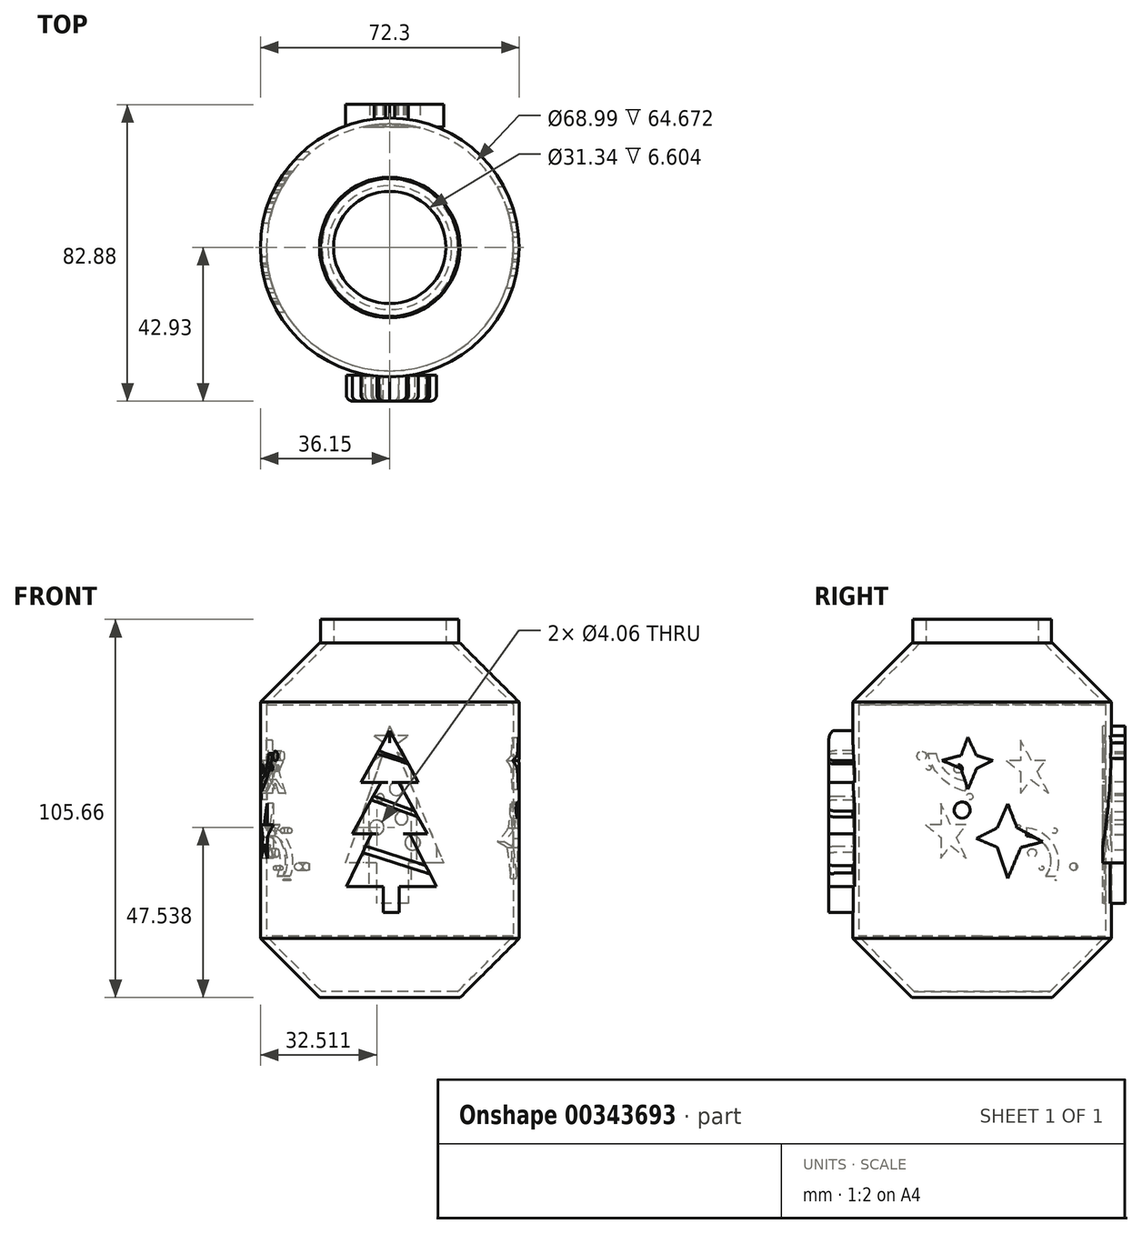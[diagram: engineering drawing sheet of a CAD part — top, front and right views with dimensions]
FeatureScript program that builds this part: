
annotation { "Feature Type Name" : "Feature", "Feature Type Description" : "" }
export const myFeature = defineFeature(function(context is Context, id is Id, definition is map)
    precondition{}
    {
        {
            var Q0;
            Q0=qCreatedBy(makeId("Top.planeOp"),FACE);
            var sketch = newSketch(context, id + "F0", { "sketchPlane" : qUnion([Q0])});
            skCircle(sketch, "E0", {"center": v(0, 0) * mm, "radius": 27.8 * mm});
            skSolve(sketch);
        }
        {
            var Q0;
            Q0=makeQuery(id+"F0.imprint","IMPRINT",FACE,{"disambiguationData":[TD([[makeQuery(id+"F0.imprint","IMPRINT",EDGE,{"derivedFrom":sQuery(id+"F0.wireOp",EDGE,"E0")}),1.0]])]});
            extrude(context, id + "F1", {"entities" : qUnion([Q0]), "depth" : 76.2 * mm});
        }
        {
            var Q0;
            Q0=makeQuery(id+"F1.opExtrude","CAP_EDGE",EDGE,{"disambiguationData":[OSD([sQuery(id+"F0.wireOp",EDGE,"E0")])],"isStart":false});
            var Q1;
            Q1=makeQuery(id+"F1.opExtrude","SWEPT_FACE",FACE,{"disambiguationData":[OSD([sQuery(id+"F0.wireOp",EDGE,"E0")])]});
            chamfer(context, id + "F2", {"entities" : qUnion([Q0, Q1]), "width" : 12.7 * mm, "tangentPropagation" : true});
        }
        {
            var Q0;
            Q0=makeQuery(id+"F1.opExtrude","CAP_FACE",FACE,{"disambiguationData":[OSD([sQuery(id+"F0.wireOp",EDGE,"E0")])],"isStart":false});
            shell(context, id + "F3", {"entities" : qUnion([Q0]), "thickness" : 1.27 * mm});
        }
        {
            var Q0;
            Q0=qCreatedBy(makeId("Front.planeOp"),FACE);
            cPlane(context, id + "F4", {"entities" : qUnion([Q0]), "cplaneType" : CPlaneType.OFFSET, "offset" : 27.43 * mm, "width" : 152.4 * mm, "height" : 152.4 * mm});
        }
        {
            var Q0;
            Q0=qCreatedBy(id+"F4.planeOp",FACE);
            var sketch = newSketch(context, id + "F5", { "sketchPlane" : qUnion([Q0])});
            skLineSegment(sketch, "E1", {"start": v(0, 57.39) * mm, "end": v(-6.16, 46.28) * mm});
            skLineSegment(sketch, "E2", {"start": v(-6.16, 46.28) * mm, "end": v(-1.9, 46.28) * mm});
            skLineSegment(sketch, "E3", {"start": v(6.16, 46.28) * mm, "end": v(0, 57.39) * mm});
            skLineSegment(sketch, "E4", {"start": v(-1.9, 46.28) * mm, "end": v(-8.05, 35.18) * mm});
            skLineSegment(sketch, "E5", {"start": v(-8.05, 35.18) * mm, "end": v(-3.9, 35.18) * mm});
            skLineSegment(sketch, "E6", {"start": v(8.05, 35.18) * mm, "end": v(1.9, 46.28) * mm});
            skPoint(sketch, "E7.orphan", {"position": v(0, 49.7) * mm});
            skLineSegment(sketch, "E8.trimOffspring", {"start": v(1.9, 46.28) * mm, "end": v(6.16, 46.28) * mm});
            skLineSegment(sketch, "E9", {"start": v(-3.9, 35.18) * mm, "end": v(-9.31, 23.85) * mm});
            skLineSegment(sketch, "E10", {"start": v(4.3, 35.18) * mm, "end": v(10.03, 23.85) * mm});
            skLineSegment(sketch, "E11", {"start": v(10.03, 23.85) * mm, "end": v(2.04, 23.85) * mm});
            skLineSegment(sketch, "E12.trimOffspring", {"start": v(4.3, 35.18) * mm, "end": v(8.05, 35.18) * mm});
            skLineSegment(sketch, "E13.top", {"start": v(2.04, 18.3) * mm, "end": v(-1.34, 18.3) * mm});
            skLineSegment(sketch, "E13.left", {"start": v(2.04, 23.85) * mm, "end": v(2.04, 18.3) * mm});
            skLineSegment(sketch, "E13.right", {"start": v(-1.34, 23.85) * mm, "end": v(-1.34, 18.3) * mm});
            skLineSegment(sketch, "E14.trimOffspring", {"start": v(-1.34, 23.85) * mm, "end": v(-9.31, 23.85) * mm});
            skSolve(sketch);
        }
        {
            var Q0;
            Q0 = qSketchRegion(id + "F5", true);
            extrude(context, id + "F6", {"entities" : qUnion([Q0]), "operationType" : NewBodyOperationType.ADD, "depth" : 5.6 * mm});
        }
        {
            var Q0;
            Q0=makeQuery(id+"F6.opExtrude","CAP_EDGE",EDGE,{"disambiguationData":[OSD([sQuery(id+"F5.wireOp",EDGE,"E3")])],"isStart":false});
            var Q1;
            Q1=makeQuery(id+"F6.opExtrude","CAP_EDGE",EDGE,{"disambiguationData":[OSD([sQuery(id+"F5.wireOp",EDGE,"E1")])],"isStart":false});
            var Q2;
            Q2=makeQuery(id+"F6.opExtrude","CAP_EDGE",EDGE,{"disambiguationData":[OSD([sQuery(id+"F5.wireOp",EDGE,"E9")])],"isStart":false});
            var Q3;
            Q3=makeQuery(id+"F6.opExtrude","CAP_EDGE",EDGE,{"disambiguationData":[OSD([sQuery(id+"F5.wireOp",EDGE,"E4")])],"isStart":false});
            var Q4;
            Q4=makeQuery(id+"F6.opExtrude","CAP_EDGE",EDGE,{"disambiguationData":[OSD([sQuery(id+"F5.wireOp",EDGE,"E6")])],"isStart":false});
            var Q5;
            Q5=makeQuery(id+"F6.opExtrude","CAP_EDGE",EDGE,{"disambiguationData":[OSD([sQuery(id+"F5.wireOp",EDGE,"E10")])],"isStart":false});
            fillet(context, id + "F7", {"entities" : qUnion([Q0, Q1, Q2, Q3, Q4, Q5]), "radius" : 1.27 * mm, "tangentPropagation" : true, "allowEdgeOverflow" : false});
        }
        {
            var Q0;
            Q0=qCreatedBy(id+"F4.planeOp",FACE);
            var Q1;
            Q1 = qBodyType(qCreatedBy(id + "F9" ,EDGE), BodyType.WIRE);
            cPlane(context, id + "F8", {"entities" : qUnion([Q0, Q1]), "cplaneType" : CPlaneType.OFFSET, "offset" : 5.84 * mm, "width" : 152.4 * mm, "height" : 152.4 * mm});
        }
        {
            var Q0;
            Q0=qCreatedBy(id+"F8.planeOp",FACE);
            var sketch = newSketch(context, id + "F9", { "sketchPlane" : qUnion([Q0])});
            skLineSegment(sketch, "E15", {"start": v(-2.4, 53.07) * mm, "end": v(3.58, 50.94) * mm});
            skLineSegment(sketch, "E16", {"start": v(3.58, 50.94) * mm, "end": v(4, 50.2) * mm});
            skLineSegment(sketch, "E17", {"start": v(4, 50.2) * mm, "end": v(-2.76, 52.43) * mm});
            skLineSegment(sketch, "E18", {"start": v(-2.76, 52.43) * mm, "end": v(-2.4, 53.07) * mm});
            skLineSegment(sketch, "E19.0", {"start": v(0, 57.39) * mm, "end": v(6.16, 46.28) * mm});
            skLineSegment(sketch, "E20", {"start": v(-3.54, 43.37) * mm, "end": v(5.35, 40.1) * mm});
            skLineSegment(sketch, "E21", {"start": v(5.35, 40.1) * mm, "end": v(6.1, 38.81) * mm});
            skLineSegment(sketch, "E22", {"start": v(6.1, 38.81) * mm, "end": v(-4.02, 42.49) * mm});
            skLineSegment(sketch, "E23", {"start": v(-4.02, 42.49) * mm, "end": v(-3.54, 43.37) * mm});
            skLineSegment(sketch, "E24", {"start": v(-5.18, 32.56) * mm, "end": v(7.86, 28.32) * mm});
            skLineSegment(sketch, "E25", {"start": v(7.86, 28.32) * mm, "end": v(8.64, 26.56) * mm});
            skLineSegment(sketch, "E26", {"start": v(8.64, 26.56) * mm, "end": v(-5.84, 31.16) * mm});
            skLineSegment(sketch, "E27", {"start": v(-5.84, 31.16) * mm, "end": v(-5.18, 32.56) * mm});
            skSolve(sketch);
        }
        {
            var Q0;
            Q0 = qSketchRegion(id + "F9", true);
            extrude(context, id + "F10", {"entities" : qUnion([Q0]), "operationType" : NewBodyOperationType.REMOVE, "oppositeDirection" : true, "depth" : 5.6 * mm});
        }
        {
            var Q0;
            Q0=qCreatedBy(makeId("Right.planeOp"),FACE);
            cPlane(context, id + "F11", {"entities" : qUnion([Q0]), "cplaneType" : CPlaneType.OFFSET, "offset" : 28.2 * mm, "width" : 152.4 * mm, "height" : 152.4 * mm});
        }
        {
            var Q0;
            Q0=qCreatedBy(id+"F11.planeOp",FACE);
            var sketch = newSketch(context, id + "F12", { "sketchPlane" : qUnion([Q0])});
            skLineSegment(sketch, "E28", {"start": v(-3.07, 55.96) * mm, "end": v(-4.52, 52.05) * mm});
            skLineSegment(sketch, "E29", {"start": v(-4.52, 52.05) * mm, "end": v(-8.66, 50.98) * mm});
            skLineSegment(sketch, "E30", {"start": v(-8.66, 50.98) * mm, "end": v(-4.52, 49.22) * mm});
            skLineSegment(sketch, "E31", {"start": v(-4.52, 49.22) * mm, "end": v(-3.07, 44.74) * mm});
            skLineSegment(sketch, "E32", {"start": v(-3.07, 44.74) * mm, "end": v(-1.23, 49.22) * mm});
            skLineSegment(sketch, "E33", {"start": v(-1.23, 49.22) * mm, "end": v(2.26, 50.98) * mm});
            skLineSegment(sketch, "E34", {"start": v(2.26, 50.98) * mm, "end": v(-1.23, 52.05) * mm});
            skLineSegment(sketch, "E35", {"start": v(-1.23, 52.05) * mm, "end": v(-3.07, 55.96) * mm});
            skLineSegment(sketch, "E36", {"start": v(5.5, 41.67) * mm, "end": v(3.3, 36.5) * mm});
            skLineSegment(sketch, "E37", {"start": v(3.3, 36.5) * mm, "end": v(-1.23, 34.22) * mm});
            skLineSegment(sketch, "E38", {"start": v(-1.23, 34.22) * mm, "end": v(3.3, 32.29) * mm});
            skLineSegment(sketch, "E39", {"start": v(3.3, 32.29) * mm, "end": v(5.5, 25.62) * mm});
            skLineSegment(sketch, "E40", {"start": v(5.5, 25.62) * mm, "end": v(8.34, 32.29) * mm});
            skLineSegment(sketch, "E41", {"start": v(8.34, 32.29) * mm, "end": v(13.05, 33.5) * mm});
            skLineSegment(sketch, "E42", {"start": v(13.05, 33.5) * mm, "end": v(7.5, 36.5) * mm});
            skLineSegment(sketch, "E43", {"start": v(7.5, 36.5) * mm, "end": v(5.5, 41.67) * mm});
            skCircle(sketch, "E44", {"center": v(-4.3, 40.3) * mm, "radius": 1.73 * mm});
            skSolve(sketch);
        }
        {
            var Q0;
            Q0 = qSketchRegion(id + "F12", true);
            extrude(context, id + "F13", {"entities" : qUnion([Q0]), "operationType" : NewBodyOperationType.REMOVE, "oppositeDirection" : true, "depth" : 6.1 * mm});
        }
        {
            var Q0;
            Q0=qCreatedBy(makeId("Front.planeOp"),FACE);
            cPlane(context, id + "F14", {"entities" : qUnion([Q0]), "cplaneType" : CPlaneType.OFFSET, "offset" : 25.9 * mm, "oppositeDirection" : true, "width" : 152.4 * mm, "height" : 152.4 * mm});
        }
        {
            var Q0;
            Q0=qCreatedBy(id+"F14.planeOp",FACE);
            var sketch = newSketch(context, id + "F15", { "sketchPlane" : qUnion([Q0])});
            skLineSegment(sketch, "E45", {"start": v(1.57, 52.8) * mm, "end": v(11.56, 28.93) * mm});
            skLineSegment(sketch, "E46", {"start": v(11.56, 28.93) * mm, "end": v(-9.45, 28.93) * mm});
            skLineSegment(sketch, "E47", {"start": v(-9.45, 28.93) * mm, "end": v(-1.42, 52.39) * mm});
            skLineSegment(sketch, "E48", {"start": v(3.93, 28.93) * mm, "end": v(3.93, 20.27) * mm});
            skLineSegment(sketch, "E49", {"start": v(3.93, 20.27) * mm, "end": v(-2.85, 20.27) * mm});
            skLineSegment(sketch, "E50", {"start": v(-2.85, 20.27) * mm, "end": v(-2.85, 28.93) * mm});
            skLineSegment(sketch, "E51", {"start": v(4, 56.28) * mm, "end": v(1.06, 56.28) * mm});
            skLineSegment(sketch, "E52", {"start": v(-3.36, 56.28) * mm, "end": v(-1.5, 54.97) * mm});
            skLineSegment(sketch, "E53", {"start": v(3.54, 51.4) * mm, "end": v(1.85, 54.74) * mm});
            skLineSegment(sketch, "E54", {"start": v(0, 58.36) * mm, "end": v(-0.92, 56.28) * mm});
            skLineSegment(sketch, "E55", {"start": v(-3.2, 51.1) * mm, "end": v(-1.42, 52.39) * mm});
            skLineSegment(sketch, "E56.trimOffspring", {"start": v(1.06, 56.28) * mm, "end": v(0, 58.36) * mm});
            skLineSegment(sketch, "E57.trimOffspring", {"start": v(-0.92, 56.28) * mm, "end": v(-3.36, 56.28) * mm});
            skPoint(sketch, "E58.orphan", {"position": v(0, 56.54) * mm});
            skLineSegment(sketch, "E59.trimOffspring", {"start": v(-1.5, 54.97) * mm, "end": v(-3.2, 51.1) * mm});
            skLineSegment(sketch, "E60.trimOffspring", {"start": v(1.57, 52.8) * mm, "end": v(3.54, 51.4) * mm});
            skLineSegment(sketch, "E61.trimOffspring", {"start": v(1.85, 54.74) * mm, "end": v(4, 56.28) * mm});
            skCircle(sketch, "E62", {"center": v(1.43, 44.91) * mm, "radius": 1.47 * mm});
            skCircle(sketch, "E63", {"center": v(-2.8, 36.57) * mm, "radius": 1.56 * mm});
            skCircle(sketch, "E64", {"center": v(4.9, 33.32) * mm, "radius": 1.61 * mm});
            skCircle(sketch, "E65", {"center": v(2.51, 38.52) * mm, "radius": 1.37 * mm});
            skCircle(sketch, "E66", {"center": v(-2.03, 43) * mm, "radius": 0.81 * mm});
            skSolve(sketch);
        }
        {
            var Q0;
            Q0 = qSketchRegion(id + "F15", true);
            extrude(context, id + "F16", {"entities" : qUnion([Q0]), "operationType" : NewBodyOperationType.ADD, "oppositeDirection" : true, "depth" : 4.83 * mm});
        }
        {
            var Q0;
            Q0=qCreatedBy(makeId("Right.planeOp"),FACE);
            cPlane(context, id + "F17", {"entities" : qUnion([Q0]), "cplaneType" : CPlaneType.OFFSET, "offset" : 27.94 * mm, "oppositeDirection" : true, "width" : 152.4 * mm, "height" : 152.4 * mm});
        }
        {
            var Q0;
            Q0=qCreatedBy(id+"F17.planeOp",FACE);
            var sketch = newSketch(context, id + "F18", { "sketchPlane" : qUnion([Q0])});
            skLineSegment(sketch, "E67", {"start": v(5.15, 50.93) * mm, "end": v(8.21, 50.93) * mm});
            skLineSegment(sketch, "E68", {"start": v(13.58, 50.93) * mm, "end": v(11.82, 48.61) * mm});
            skLineSegment(sketch, "E69", {"start": v(8.21, 43.88) * mm, "end": v(8.21, 48.58) * mm});
            skLineSegment(sketch, "E70", {"start": v(8.21, 55.37) * mm, "end": v(10.58, 50.93) * mm});
            skLineSegment(sketch, "E71", {"start": v(14.34, 43.88) * mm, "end": v(10.47, 46.85) * mm});
            skLineSegment(sketch, "E72", {"start": v(-12.17, 37.13) * mm, "end": v(-8.9, 37.13) * mm});
            skLineSegment(sketch, "E73", {"start": v(-3.44, 37.13) * mm, "end": v(-5.5, 34.42) * mm});
            skLineSegment(sketch, "E74", {"start": v(-8.9, 29.96) * mm, "end": v(-8.9, 34.44) * mm});
            skLineSegment(sketch, "E75", {"start": v(-8.9, 41.73) * mm, "end": v(-6.76, 37.13) * mm});
            skLineSegment(sketch, "E76", {"start": v(-3.44, 29.96) * mm, "end": v(-6.8, 32.72) * mm});
            skLineSegment(sketch, "E77.trimOffspring", {"start": v(11.82, 48.61) * mm, "end": v(14.34, 43.88) * mm});
            skLineSegment(sketch, "E78.trimOffspring", {"start": v(10.58, 50.93) * mm, "end": v(13.58, 50.93) * mm});
            skLineSegment(sketch, "E79.trimOffspring", {"start": v(8.21, 50.93) * mm, "end": v(8.21, 55.37) * mm});
            skLineSegment(sketch, "E80.trimOffspring", {"start": v(8.21, 48.58) * mm, "end": v(5.15, 50.93) * mm});
            skLineSegment(sketch, "E81.trimOffspring", {"start": v(10.47, 46.85) * mm, "end": v(8.21, 43.88) * mm});
            skLineSegment(sketch, "E82.trimOffspring", {"start": v(-6.76, 37.13) * mm, "end": v(-3.44, 37.13) * mm});
            skLineSegment(sketch, "E83.trimOffspring", {"start": v(-5.5, 34.42) * mm, "end": v(-3.44, 29.96) * mm});
            skLineSegment(sketch, "E84.trimOffspring", {"start": v(-6.8, 32.72) * mm, "end": v(-8.9, 29.96) * mm});
            skLineSegment(sketch, "E85.trimOffspring", {"start": v(-8.9, 34.44) * mm, "end": v(-12.17, 37.13) * mm});
            skLineSegment(sketch, "E86.trimOffspring", {"start": v(-8.9, 37.13) * mm, "end": v(-8.9, 41.73) * mm});
            skArc(sketch, "E87", {"start": v(-9.8, 52.5) * mm, "mid": v(-7.7, 48.55) * mm, "end": v(-3.73, 46.52) * mm});
            skArc(sketch, "E88", {"start": v(-9.8, 52.5) * mm, "mid": v(-10.73, 52.55) * mm, "end": v(-11.65, 52.5) * mm});
            skArc(sketch, "E89", {"start": v(-3.73, 44.35) * mm, "mid": v(-3.55, 45.44) * mm, "end": v(-3.73, 46.52) * mm});
            skArc(sketch, "E90", {"start": v(-11.65, 52.5) * mm, "mid": v(-8.83, 47.3) * mm, "end": v(-3.73, 44.35) * mm});
            skArc(sketch, "E91", {"start": v(15.72, 26.16) * mm, "mid": v(15.3, 32.97) * mm, "end": v(9.51, 36.59) * mm});
            skLineSegment(sketch, "E92", {"start": v(9.51, 36.59) * mm, "end": v(9.51, 34.73) * mm});
            skLineSegment(sketch, "E93", {"start": v(15.72, 26.16) * mm, "end": v(13.63, 26.16) * mm});
            skArc(sketch, "E94", {"start": v(13.63, 26.16) * mm, "mid": v(14.19, 31.7) * mm, "end": v(9.51, 34.73) * mm});
            skArc(sketch, "E95", {"start": v(15.74, 25.4) * mm, "mid": v(15.78, 25.27) * mm, "end": v(15.84, 25.14) * mm});
            skPoint(sketch, "E96.center.orphan", {"position": v(-14.08, 54.82) * mm});
            skPoint(sketch, "E97.center.orphan", {"position": v(-11.9, 54.82) * mm});
            skPoint(sketch, "E98.center.orphan", {"position": v(-9.8, 54.28) * mm});
            skArc(sketch, "E99.trimOffspring", {"start": v(15.84, 25.14) * mm, "mid": v(15.8, 25.28) * mm, "end": v(15.74, 25.4) * mm});
            skCircle(sketch, "E100", {"center": v(12.76, 27.85) * mm, "radius": 0.47 * mm});
            skCircle(sketch, "E101", {"center": v(15.55, 35.88) * mm, "radius": 0.59 * mm});
            skCircle(sketch, "E102", {"center": v(7.86, 36.78) * mm, "radius": 0.36 * mm});
            skCircle(sketch, "E103", {"center": v(19.68, 28.14) * mm, "radius": 0.8 * mm});
            skCircle(sketch, "E104", {"center": v(10.73, 31.1) * mm, "radius": 0.92 * mm});
            skCircle(sketch, "E105", {"center": v(-5.13, 49.15) * mm, "radius": 0.9 * mm});
            skCircle(sketch, "E106", {"center": v(-11.5, 49.4) * mm, "radius": 0.52 * mm});
            skCircle(sketch, "E107", {"center": v(-12.99, 51.94) * mm, "radius": 1.01 * mm});
            skCircle(sketch, "E108", {"center": v(-2.7, 43.2) * mm, "radius": 0.7 * mm});
            skSolve(sketch);
        }
        {
            var Q0;
            Q0 = qSketchRegion(id + "F18", true);
            extrude(context, id + "F19", {"entities" : qUnion([Q0]), "operationType" : NewBodyOperationType.REMOVE, "depth" : 10.67 * mm});
        }
        {
            var Q0;
            Q0=qCreatedBy(id+"F14.planeOp",FACE);
            var sketch = newSketch(context, id + "F20", { "sketchPlane" : qUnion([Q0])});
            skCircle(sketch, "E109.0", {"center": v(-2.03, 43) * mm, "radius": 0.81 * mm});
            skCircle(sketch, "E110.0", {"center": v(1.43, 44.91) * mm, "radius": 1.47 * mm});
            skCircle(sketch, "E111.0", {"center": v(2.51, 38.52) * mm, "radius": 1.37 * mm});
            skCircle(sketch, "E112.0", {"center": v(-2.8, 36.57) * mm, "radius": 1.56 * mm});
            skCircle(sketch, "E113.0", {"center": v(4.9, 33.32) * mm, "radius": 1.61 * mm});
            skSolve(sketch);
        }
        {
            var Q0;
            Q0 = qSketchRegion(id + "F20", true);
            extrude(context, id + "F21", {"entities" : qUnion([Q0]), "operationType" : NewBodyOperationType.REMOVE, "depth" : 7.62 * mm});
        }
        {
            var Q0;
            Q0=qCreatedBy(makeId("Top.planeOp"),FACE);
            cPlane(context, id + "F22", {"entities" : qUnion([Q0]), "cplaneType" : CPlaneType.OFFSET, "offset" : 76.2 * mm, "width" : 152.4 * mm, "height" : 152.4 * mm});
        }
        {
            var Q0;
            Q0=qCreatedBy(id+"F22.planeOp",FACE);
            var sketch = newSketch(context, id + "F23", { "sketchPlane" : qUnion([Q0])});
            skCircle(sketch, "E114", {"center": v(0, 0) * mm, "radius": 12.06 * mm});
            skCircle(sketch, "E115", {"center": v(0, 0) * mm, "radius": 14.86 * mm});
            skSolve(sketch);
        }
        {
            var Q0;
            Q0 = qSketchRegion(id + "F23", true);
            extrude(context, id + "F24", {"entities" : qUnion([Q0]), "operationType" : NewBodyOperationType.ADD, "depth" : 5.08 * mm});
        }
        {
            var Q0;
            Q0=makeQuery(id+"F1.opExtrude","SWEPT_BODY",BODY,{"disambiguationData":[OSD([sQuery(id+"F0.wireOp",EDGE,"E0")])]});
            var Q1;
            Q1=qCreatedBy(makeId("Origin.pointOp"),VERTEX);
            transform(context, id + "F25", {"entities" : qUnion([Q0]), "transformType" : TransformType.SCALE_UNIFORMLY, "scale" : 1.3, "scalePoint" : qUnion([Q1]), "makeCopy" : false});
        }
    });
